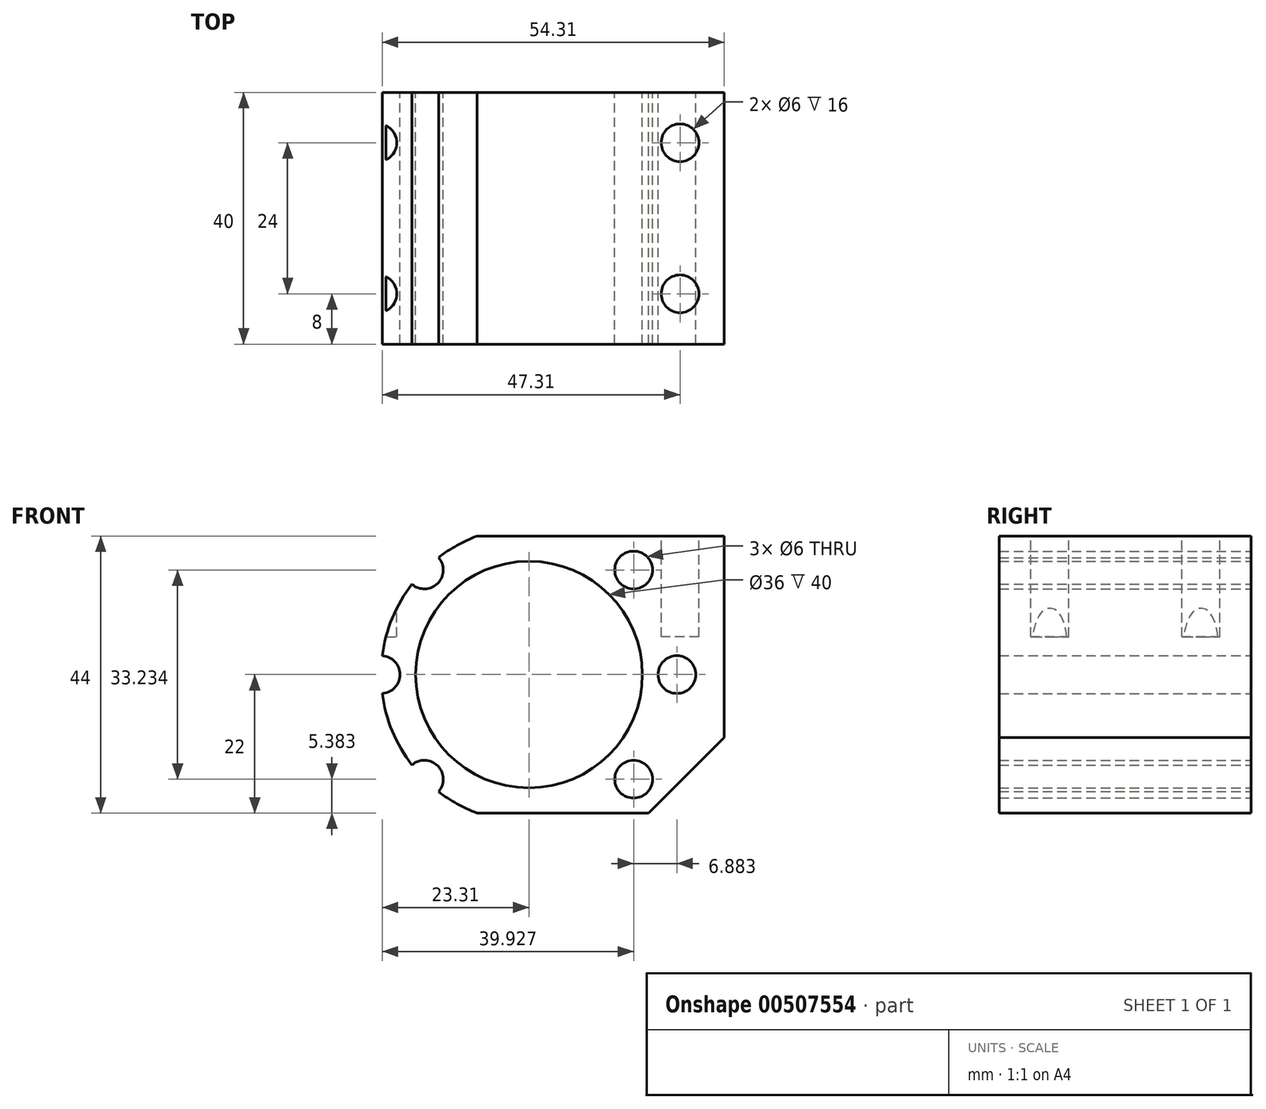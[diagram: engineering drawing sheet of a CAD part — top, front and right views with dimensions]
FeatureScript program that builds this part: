
annotation { "Feature Type Name" : "Feature", "Feature Type Description" : "" }
export const myFeature = defineFeature(function(context is Context, id is Id, definition is map)
    precondition{}
    {
        {
            var Q0;
            Q0=qCreatedBy(makeId("Front.planeOp"),FACE);
            var sketch = newSketch(context, id + "F0", { "sketchPlane" : qUnion([Q0])});
            skLineSegment(sketch, "E0.bottom", {"start": v(12, 0) * mm, "end": v(50, 0) * mm});
            skLineSegment(sketch, "E0.top", {"start": v(0, 44) * mm, "end": v(62, 44) * mm});
            skLineSegment(sketch, "E0.left", {"start": v(0, 12) * mm, "end": v(0, 44) * mm});
            skLineSegment(sketch, "E0.right", {"start": v(62, 12) * mm, "end": v(62, 44) * mm});
            skLineSegment(sketch, "E1", {"start": v(0, 44) * mm, "end": v(0, 12) * mm});
            skLineSegment(sketch, "E2", {"start": v(0, 12) * mm, "end": v(12, 0) * mm});
            skLineSegment(sketch, "E3", {"start": v(50, 0) * mm, "end": v(62, 12) * mm});
            skPoint(sketch, "E4.orphan", {"position": v(0, 0) * mm});
            skCircle(sketch, "E5", {"center": v(31, 22) * mm, "radius": 18 * mm});
            skArc(sketch, "E6", {"start": v(12.4, 36.36) * mm, "mid": v(9.29, 31) * mm, "end": v(7.7, 25) * mm});
            skCircle(sketch, "E7", {"center": v(54.5, 22) * mm, "radius": 3 * mm});
            skCircle(sketch, "E8", {"center": v(7.5, 22) * mm, "radius": 3 * mm});
            skLineSegment(sketch, "E9", {"start": v(10.5, 22) * mm, "end": v(31, 22) * mm});
            skLineSegment(sketch, "E10", {"start": v(31, 22) * mm, "end": v(16.5, 36.5) * mm});
            skCircle(sketch, "E11", {"center": v(14.38, 38.62) * mm, "radius": 3 * mm});
            skCircle(sketch, "E12", {"center": v(14.38, 5.38) * mm, "radius": 3 * mm});
            skCircle(sketch, "E13", {"center": v(47.62, 38.62) * mm, "radius": 3 * mm});
            skCircle(sketch, "E14", {"center": v(47.62, 5.38) * mm, "radius": 3 * mm});
            skLineSegment(sketch, "E15.trimOffspring", {"start": v(12.26, 40.74) * mm, "end": v(12.04, 40.96) * mm});
            skArc(sketch, "E16.trimOffspring", {"start": v(45.36, 40.6) * mm, "mid": v(42.44, 42.53) * mm, "end": v(39.26, 44) * mm});
            skArc(sketch, "E17.trimOffspring", {"start": v(54.3, 25) * mm, "mid": v(52.71, 31) * mm, "end": v(49.6, 36.36) * mm});
            skArc(sketch, "E18.trimOffspring", {"start": v(49.6, 7.64) * mm, "mid": v(52.71, 13) * mm, "end": v(54.3, 19) * mm});
            skArc(sketch, "E19.trimOffspring", {"start": v(7.7, 19) * mm, "mid": v(9.29, 13) * mm, "end": v(12.4, 7.64) * mm});
            skArc(sketch, "E20.trimOffspring", {"start": v(16.64, 3.4) * mm, "mid": v(19.56, 1.47) * mm, "end": v(22.74, 0) * mm});
            skArc(sketch, "E21.trimOffspring", {"start": v(39.26, 0) * mm, "mid": v(42.44, 1.47) * mm, "end": v(45.36, 3.4) * mm});
            skArc(sketch, "E22.trimOffspring", {"start": v(22.74, 44) * mm, "mid": v(19.56, 42.53) * mm, "end": v(16.64, 40.6) * mm});
            skSolve(sketch);
        }
        {
            var Q0;
            {var subQ4=sQuery(id+"F0.wireOp",EDGE,"E1");Q0=makeQuery(id+"F0.imprint","IMPRINT",FACE,{"disambiguationData":[TD([[makeQuery(id+"F0.imprint","IMPRINT",EDGE,{"derivedFrom":subQ4}),1.0]])]});}
            var Q1;
            {var subQ5=sQuery(id+"F0.wireOp",EDGE,"E6");Q1=makeQuery(id+"F0.imprint","IMPRINT",FACE,{"disambiguationData":[TD([[makeQuery(id+"F0.imprint","IMPRINT",EDGE,{"derivedFrom":subQ5}),1.0]])]});}
            var Q2;
            {var subQ13=sQuery(id+"F0.wireOp",EDGE,"E16.trimOffspring");Q2=makeQuery(id+"F0.imprint","IMPRINT",FACE,{"disambiguationData":[TD([[makeQuery(id+"F0.imprint","IMPRINT",EDGE,{"derivedFrom":subQ13}),1.0]])]});}
            var Q3;
            {var subQ8=sQuery(id+"F0.wireOp",EDGE,"E3");Q3=makeQuery(id+"F0.imprint","IMPRINT",FACE,{"disambiguationData":[TD([[makeQuery(id+"F0.imprint","IMPRINT",EDGE,{"derivedFrom":subQ8}),1.0]])]});}
            extrude(context, id + "F1", {"entities" : qUnion([Q0, Q1, Q2, Q3]), "depth" : 40 * mm, "offsetDistance" : 25 * mm});
        }
        {
            var Q0;
            Q0=makeQuery(id+"F1.opExtrude","SWEPT_FACE",FACE,{"disambiguationData":[OSD([sQuery(id+"F0.wireOp",EDGE,"E0.top")])]});
            var sketch = newSketch(context, id + "F2", { "sketchPlane" : qUnion([Q0])});
            skCircle(sketch, "E23", {"center": v(7, -8) * mm, "radius": 3 * mm});
            skCircle(sketch, "E24", {"center": v(7, -32) * mm, "radius": 3 * mm});
            skCircle(sketch, "E25", {"center": v(55, -32) * mm, "radius": 3 * mm});
            skCircle(sketch, "E26", {"center": v(55, -8) * mm, "radius": 3 * mm});
            skSolve(sketch);
        }
        {
            var Q0;
            Q0 = qSketchRegion(id + "F2", true);
            extrude(context, id + "F3", {"entities" : qUnion([Q0]), "operationType" : NewBodyOperationType.REMOVE, "oppositeDirection" : true, "depth" : 16 * mm, "offsetDistance" : 25 * mm});
        }
    });
